FCSTD DOCUMENT  (FreeCAD 0.18R4 (GitTag))
Label: AAM6_Assembled
License: All rights reserved
LicenseURL: http://en.wikipedia.org/wiki/All_rights_reserved
objects: Part::Feature×212, Part::FeaturePython×80, App::DocumentObjectGroup×22, App::Part×19, Part::Sphere×2
note: 294 computed .brp shape members not serialized (recipe doc carries the construction recipe); baked Part::Feature solids carry a one-line shape summary decoded from their .brp

FEATURE [Part::Feature] Body001053  label="D8x380_Rod_001"
  Placement = pos=(-85,-190,7.9) rot=(-1,0,0;1.5708rad)
  shape: bbox 8 x 380 x 8 mm, 5 faces (baked)
FEATURE [Part::Feature] Body001054  label="D8x380_Rod_002"
  Placement = pos=(85,-190,7.9) rot=(-1,0,0;1.5708rad)
  shape: bbox 8 x 380 x 8 mm, 5 faces (baked)
FEATURE [Part::Feature] Body001079  label="CenterMark"
  Placement = pos=(0,-189,17.35) rot=(0,0,1;0rad)
  shape: bbox 0.2 x 390 x 80 mm, 6 faces (baked)
FEATURE [Part::Feature] Fusion011  label="EndstopSwitchY"
  Placement = pos=(64.75,176.5,8.2) rot=(0,0,1;1.5708rad)
  shape: bbox 20.93 x 24.69 x 6.4 mm, 73 faces, 2 solids (baked)
FEATURE [Part::Feature] Fusion012  label="StepperMotorNema017_Y"
  Placement = pos=(0,0,0) rot=(0,0,1;1.5708rad)
  shape: bbox 42 x 54 x 61.2 mm, 83 faces (baked)
FEATURE [Part::Feature] Body001082002  label="EndSwitchDummy"
  Placement = pos=(64.75,162.4,8) rot=(0,0,1;0rad)
  shape: bbox 20 x 17 x 1 mm, 8 faces (baked)
FEATURE [Part::Feature] Body001082005  label="L-Conn_2x2_12xD5_78x78x3_001"
  Placement = pos=(-195.5,13,419) rot=(0.57735,0.57735,-0.57735;2.0944rad)
  shape: bbox 78 x 3 x 78 mm, 24 faces (baked)
FEATURE [Part::Feature] Body001082006  label="L-Conn_2x2_12xD5_78x78x3_002"
  Placement = pos=(195.5,13,419) rot=(0,0.707107,-0.707107;3.14159rad)
  shape: bbox 78 x 3 x 78 mm, 24 faces (baked)
FEATURE [Part::Feature] Body001082007  label="L-Conn_1x1_5xD5_58x58x3_001"
  Placement = pos=(-155.5,189,-23) rot=(0,0,-1;1.5708rad)
  shape: bbox 58 x 58 x 3 mm, 17 faces (baked)
FEATURE [Part::Feature] Body001082008  label="L-Conn_1x1_5xD5_58x58x3_002"
  Placement = pos=(155.5,189,-23) rot=(0,0,1;3.14159rad)
  shape: bbox 58 x 58 x 3 mm, 17 faces (baked)
FEATURE [Part::Feature] Body001082009  label="L-Conn_1x1_5xD5_58x58x3_003"
  Placement = pos=(-155.5,-189,-23) rot=(0,1,0;0rad)
  shape: bbox 58 x 58 x 3 mm, 17 faces (baked)
FEATURE [Part::Feature] Body001082010  label="L-Conn_1x1_5xD5_58x58x3_004"
  Placement = pos=(155.5,-189,-23) rot=(0,0,1;1.5708rad)
  shape: bbox 58 x 58 x 3 mm, 17 faces (baked)
FEATURE [App::DocumentObjectGroup] Group002  label="JointsXY"
  Group = -> [Body001082007,Body001082008,Body001082009,Body001082010]
FEATURE [Part::Feature] Body001082011  label="T-Conn_1x1_5xD5_58x58x3_001"
  Placement = pos=(-137.5,3.1e-14,-23) rot=(0,0,1;1.5708rad)
  shape: bbox 58 x 58 x 3 mm, 19 faces (baked)
FEATURE [Part::Feature] Body001082012  label="T-Conn_1x1_5xD5_58x58x3_002"
  Placement = pos=(137.5,-3.1e-14,-23) rot=(0,0,-1;1.5708rad)
  shape: bbox 58 x 58 x 3 mm, 19 faces (baked)
FEATURE [Part::Feature] Body001082013  label="2040_Nut5_TypI-313_001"
  Placement = pos=(-156.5,-180,0) rot=(0,1,0;1.5708rad)
  shape: bbox 313 x 20 x 40 mm, 120 faces (baked)
FEATURE [Part::Feature] Body001082014  label="2040_Nut5_TypI-313_002"
  Placement = pos=(-156.5,180,0) rot=(0,1,0;1.5708rad)
  shape: bbox 313 x 20 x 40 mm, 120 faces (baked)
FEATURE [Part::Feature] Body001082015  label="2040_Nut5_TypI-313_003"
  Placement = pos=(-156.5,0,400) rot=(0,1,0;1.5708rad)
  shape: bbox 313 x 20 x 40 mm, 120 faces (baked)
FEATURE [Part::Feature] Body001082016  label="2040_Nut5_TypI-340_001"
  Placement = pos=(-146.5,-170,0) rot=(0.57735,-0.57735,-0.57735;4.18879rad)
  shape: bbox 20 x 340 x 40 mm, 120 faces (baked)
FEATURE [Part::Feature] Body001082017  label="2040_Nut5_TypI-340_002"
  Placement = pos=(146.5,-170,0) rot=(0.57735,-0.57735,-0.57735;4.18879rad)
  shape: bbox 20 x 340 x 40 mm, 120 faces (baked)
FEATURE [App::DocumentObjectGroup] Group001  label="ExtrusionsXY"
  Group = -> [Body001082013,Body001082014,Body001082016,Body001082017]
FEATURE [Part::Feature] Body001082018  label="2040_Nut5_TypI-440_001"
  Placement = pos=(-176.5,0,-20) rot=(0,0,1;0rad)
  shape: bbox 40 x 20 x 440 mm, 120 faces (baked)
FEATURE [Part::Feature] Body001082019  label="2040_Nut5_TypI-440_002"
  Placement = pos=(176.5,0,-20) rot=(0,0,1;0rad)
  shape: bbox 40 x 20 x 440 mm, 120 faces (baked)
FEATURE [App::DocumentObjectGroup] Group003  label="ExtrusionsXZ"
  Group = -> [Body001082015,Body001082018,Body001082019]
FEATURE [Part::Feature] Body001082020  label="ISO7380-M5x8_001"
  Placement = pos=(146.5,180,-23) rot=(1,0,0;3.14159rad)
  shape: bbox 9.5 x 9.5 x 10.75 mm, 14 faces (baked)
FEATURE [Part::Feature] Body001082021  label="ISO7380-M5x8_002"
  Placement = pos=(126.5,180,-23) rot=(1,0,0;3.14159rad)
  shape: bbox 9.5 x 9.5 x 10.75 mm, 14 faces (baked)
FEATURE [Part::Feature] Body001082022  label="ISO7380-M5x8_003"
  Placement = pos=(106.5,180,-23) rot=(1,0,0;3.14159rad)
  shape: bbox 9.5 x 9.5 x 10.75 mm, 14 faces (baked)
FEATURE [Part::Feature] Body001082023  label="ISO7380-M5x8_004"
  Placement = pos=(146.5,160,-23) rot=(1,0,0;3.14159rad)
  shape: bbox 9.5 x 9.5 x 10.75 mm, 14 faces (baked)
FEATURE [Part::Feature] Body001082024  label="ISO7380-M5x8_005"
  Placement = pos=(146.5,140,-23) rot=(1,0,0;3.14159rad)
  shape: bbox 9.5 x 9.5 x 10.75 mm, 14 faces (baked)
FEATURE [Part::Feature] Body001082025  label="ISO7380-M5x8_006"
  Placement = pos=(-106.5,180,-23) rot=(1,0,0;3.14159rad)
  shape: bbox 9.5 x 9.5 x 10.75 mm, 14 faces (baked)
FEATURE [Part::Feature] Body001082026  label="ISO7380-M5x8_007"
  Placement = pos=(-126.5,180,-23) rot=(1,0,0;3.14159rad)
  shape: bbox 9.5 x 9.5 x 10.75 mm, 14 faces (baked)
FEATURE [Part::Feature] Body001082027  label="ISO7380-M5x8_008"
  Placement = pos=(-146.5,180,-23) rot=(1,0,0;3.14159rad)
  shape: bbox 9.5 x 9.5 x 10.75 mm, 14 faces (baked)
FEATURE [Part::Feature] Body001082028  label="ISO7380-M5x8_009"
  Placement = pos=(-146.5,160,-23) rot=(1,0,0;3.14159rad)
  shape: bbox 9.5 x 9.5 x 10.75 mm, 14 faces (baked)
FEATURE [Part::Feature] Body001082029  label="ISO7380-M5x8_010"
  Placement = pos=(-146.5,140,-23) rot=(1,0,0;3.14159rad)
  shape: bbox 9.5 x 9.5 x 10.75 mm, 14 faces (baked)
FEATURE [Part::Feature] Body001082030  label="ISO7380-M5x8_021"
  Placement = pos=(146.5,20,-23) rot=(1,0,0;3.14159rad)
  shape: bbox 9.5 x 9.5 x 10.75 mm, 14 faces (baked)
FEATURE [Part::Feature] Body001082031  label="ISO7380-M5x8_022"
  Placement = pos=(186.5,0,-23) rot=(1,0,0;3.14159rad)
  shape: bbox 9.5 x 9.5 x 10.75 mm, 14 faces (baked)
FEATURE [Part::Feature] Body001082032  label="ISO7380-M5x8_023"
  Placement = pos=(166.5,0,-23) rot=(1,0,0;3.14159rad)
  shape: bbox 9.5 x 9.5 x 10.75 mm, 14 faces (baked)
FEATURE [Part::Feature] Body001082033  label="ISO7380-M5x8_024"
  Placement = pos=(146.5,0,-23) rot=(1,0,0;3.14159rad)
  shape: bbox 9.5 x 9.5 x 10.75 mm, 14 faces (baked)
FEATURE [Part::Feature] Body001082034  label="ISO7380-M5x8_025"
  Placement = pos=(146.5,-20,-23) rot=(1,0,0;3.14159rad)
  shape: bbox 9.5 x 9.5 x 10.75 mm, 14 faces (baked)
FEATURE [Part::Feature] Body001082035  label="ISO7380-M5x8_026"
  Placement = pos=(-146.5,20,-23) rot=(1,0,0;3.14159rad)
  shape: bbox 9.5 x 9.5 x 10.75 mm, 14 faces (baked)
FEATURE [Part::Feature] Body001082036  label="ISO7380-M5x8_027"
  Placement = pos=(-146.5,0,-23) rot=(1,0,0;3.14159rad)
  shape: bbox 9.5 x 9.5 x 10.75 mm, 14 faces (baked)
FEATURE [Part::Feature] Body001082037  label="ISO7380-M5x8_028"
  Placement = pos=(-166.5,0,-23) rot=(1,0,0;3.14159rad)
  shape: bbox 9.5 x 9.5 x 10.75 mm, 14 faces (baked)
FEATURE [Part::Feature] Body001082038  label="ISO7380-M5x8_029"
  Placement = pos=(-186.5,0,-23) rot=(1,0,0;3.14159rad)
  shape: bbox 9.5 x 9.5 x 10.75 mm, 14 faces (baked)
FEATURE [Part::Feature] Body001082039  label="ISO7380-M5x8_030"
  Placement = pos=(-146.5,-20,-23) rot=(1,0,0;3.14159rad)
  shape: bbox 9.5 x 9.5 x 10.75 mm, 14 faces (baked)
FEATURE [Part::Feature] Body001082040  label="ISO7380-M5x8_011"
  Placement = pos=(146.5,-140,-23) rot=(1,0,0;3.14159rad)
  shape: bbox 9.5 x 9.5 x 10.75 mm, 14 faces (baked)
FEATURE [Part::Feature] Body001082041  label="ISO7380-M5x8_012"
  Placement = pos=(146.5,-160,-23) rot=(1,0,0;3.14159rad)
  shape: bbox 9.5 x 9.5 x 10.75 mm, 14 faces (baked)
FEATURE [Part::Feature] Body001082042  label="ISO7380-M5x8_013"
  Placement = pos=(146.5,-180,-23) rot=(1,0,0;3.14159rad)
  shape: bbox 9.5 x 9.5 x 10.75 mm, 14 faces (baked)
FEATURE [Part::Feature] Body001082043  label="ISO7380-M5x8_014"
  Placement = pos=(126.5,-180,-23) rot=(1,0,0;3.14159rad)
  shape: bbox 9.5 x 9.5 x 10.75 mm, 14 faces (baked)
FEATURE [Part::Feature] Body001082044  label="ISO7380-M5x8_015"
  Placement = pos=(106.5,-180,-23) rot=(1,0,0;3.14159rad)
  shape: bbox 9.5 x 9.5 x 10.75 mm, 14 faces (baked)
FEATURE [Part::Feature] Body001082045  label="ISO7380-M5x8_016"
  Placement = pos=(-146.5,-140,-23) rot=(1,0,0;3.14159rad)
  shape: bbox 9.5 x 9.5 x 10.75 mm, 14 faces (baked)
FEATURE [Part::Feature] Body001082046  label="ISO7380-M5x8_017"
  Placement = pos=(-146.5,-160,-23) rot=(1,0,0;3.14159rad)
  shape: bbox 9.5 x 9.5 x 10.75 mm, 14 faces (baked)
FEATURE [Part::Feature] Body001082047  label="ISO7380-M5x8_018"
  Placement = pos=(-106.5,-180,-23) rot=(1,0,0;3.14159rad)
  shape: bbox 9.5 x 9.5 x 10.75 mm, 14 faces (baked)
FEATURE [Part::Feature] Body001082048  label="ISO7380-M5x8_019"
  Placement = pos=(-126.5,-180,-23) rot=(1,0,0;3.14159rad)
  shape: bbox 9.5 x 9.5 x 10.75 mm, 14 faces (baked)
FEATURE [Part::Feature] Body001082049  label="ISO7380-M5x8_020"
  Placement = pos=(-146.5,-180,-23) rot=(1,0,0;3.14159rad)
  shape: bbox 9.5 x 9.5 x 10.75 mm, 14 faces (baked)
FEATURE [Part::Feature] Body001082050  label="SlidingT-NutBlock_M5_Slot5_Typ-I_001"
  Placement = pos=(149.5,180,-18.8) rot=(0.57735,0.57735,-0.57735;4.18879rad)
  shape: bbox 12 x 7.7 x 4.6 mm, 21 faces (baked)
FEATURE [Part::Feature] Body001082051  label="SlidingT-NutBlock_M5_Slot5_Typ-I_002"
  Placement = pos=(129.5,180,-18.8) rot=(0.57735,0.57735,-0.57735;4.18879rad)
  shape: bbox 12 x 7.7 x 4.6 mm, 21 faces (baked)
FEATURE [Part::Feature] Body001082052  label="SlidingT-NutBlock_M5_Slot5_Typ-I_003"
  Placement = pos=(109.5,180,-18.8) rot=(0.57735,0.57735,-0.57735;4.18879rad)
  shape: bbox 12 x 7.7 x 4.6 mm, 21 faces (baked)
FEATURE [Part::Feature] Body001082053  label="SlidingT-NutBlock_M5_Slot5_Typ-I_004"
  Placement = pos=(-109.5,180,-18.8) rot=(0.57735,-0.57735,0.57735;4.18879rad)
  shape: bbox 12 x 7.7 x 4.6 mm, 21 faces (baked)
FEATURE [Part::Feature] Body001082054  label="SlidingT-NutBlock_M5_Slot5_Typ-I_005"
  Placement = pos=(-129.5,180,-18.8) rot=(0.57735,-0.57735,0.57735;4.18879rad)
  shape: bbox 12 x 7.7 x 4.6 mm, 21 faces (baked)
FEATURE [Part::Feature] Body001082055  label="SlidingT-NutBlock_M5_Slot5_Typ-I_006"
  Placement = pos=(-149.5,180,-18.8) rot=(0.57735,-0.57735,0.57735;4.18879rad)
  shape: bbox 12 x 7.7 x 4.6 mm, 21 faces (baked)
FEATURE [Part::Feature] Body001082056  label="SlidingT-NutBlock_M5_Slot5_Typ-I_007"
  Placement = pos=(149.5,-180,-18.8) rot=(0.57735,0.57735,-0.57735;4.18879rad)
  shape: bbox 12 x 7.7 x 4.6 mm, 21 faces (baked)
FEATURE [Part::Feature] Body001082057  label="SlidingT-NutBlock_M5_Slot5_Typ-I_008"
  Placement = pos=(129.5,-180,-18.8) rot=(0.57735,0.57735,-0.57735;4.18879rad)
  shape: bbox 12 x 7.7 x 4.6 mm, 21 faces (baked)
FEATURE [Part::Feature] Body001082058  label="SlidingT-NutBlock_M5_Slot5_Typ-I_009"
  Placement = pos=(109.5,-180,-18.8) rot=(0.57735,0.57735,-0.57735;4.18879rad)
  shape: bbox 12 x 7.7 x 4.6 mm, 21 faces (baked)
FEATURE [Part::Feature] Body001082059  label="SlidingT-NutBlock_M5_Slot5_Typ-I_010"
  Placement = pos=(-109.5,-180,-18.8) rot=(0.57735,-0.57735,0.57735;4.18879rad)
  shape: bbox 12 x 7.7 x 4.6 mm, 21 faces (baked)
FEATURE [Part::Feature] Body001082060  label="SlidingT-NutBlock_M5_Slot5_Typ-I_011"
  Placement = pos=(-129.5,-180,-18.8) rot=(0.57735,-0.57735,0.57735;4.18879rad)
  shape: bbox 12 x 7.7 x 4.6 mm, 21 faces (baked)
FEATURE [Part::Feature] Body001082061  label="SlidingT-NutBlock_M5_Slot5_Typ-I_012"
  Placement = pos=(-149.5,-180,-18.8) rot=(0.57735,-0.57735,0.57735;4.18879rad)
  shape: bbox 12 x 7.7 x 4.6 mm, 21 faces (baked)
FEATURE [Part::Feature] Body001082062  label="SlidingT-NutBlock_M5_Slot5_Typ-I_013"
  Placement = pos=(146.5,163,-18.8) rot=(0,0.707107,-0.707107;3.14159rad)
  shape: bbox 7.7 x 12 x 4.6 mm, 21 faces (baked)
FEATURE [Part::Feature] Body001082063  label="SlidingT-NutBlock_M5_Slot5_Typ-I_014"
  Placement = pos=(146.5,143,-18.8) rot=(0,0.707107,-0.707107;3.14159rad)
  shape: bbox 7.7 x 12 x 4.6 mm, 21 faces (baked)
FEATURE [Part::Feature] Body001082064  label="SlidingT-NutBlock_M5_Slot5_Typ-I_015"
  Placement = pos=(-146.5,163,-18.8) rot=(0,-0.707107,0.707107;3.14159rad)
  shape: bbox 7.7 x 12 x 4.6 mm, 21 faces (baked)
FEATURE [Part::Feature] Body001082065  label="SlidingT-NutBlock_M5_Slot5_Typ-I_016"
  Placement = pos=(-146.5,143,-18.8) rot=(0,0.707107,-0.707107;3.14159rad)
  shape: bbox 7.7 x 12 x 4.6 mm, 21 faces (baked)
FEATURE [Part::Feature] Body001082066  label="SlidingT-NutBlock_M5_Slot5_Typ-I_017"
  Placement = pos=(146.5,-143,-18.8) rot=(-1,0,0;1.5708rad)
  shape: bbox 7.7 x 12 x 4.6 mm, 21 faces (baked)
FEATURE [Part::Feature] Body001082067  label="SlidingT-NutBlock_M5_Slot5_Typ-I_018"
  Placement = pos=(146.5,-163,-18.8) rot=(-1,0,0;1.5708rad)
  shape: bbox 7.7 x 12 x 4.6 mm, 21 faces (baked)
FEATURE [Part::Feature] Body001082068  label="SlidingT-NutBlock_M5_Slot5_Typ-I_019"
  Placement = pos=(-146.5,-143,-18.8) rot=(-1,0,0;1.5708rad)
  shape: bbox 7.7 x 12 x 4.6 mm, 21 faces (baked)
FEATURE [Part::Feature] Body001082069  label="SlidingT-NutBlock_M5_Slot5_Typ-I_020"
  Placement = pos=(-146.5,-163,-18.8) rot=(-1,0,0;1.5708rad)
  shape: bbox 7.7 x 12 x 4.6 mm, 21 faces (baked)
FEATURE [App::DocumentObjectGroup] Group  label="Screws&NutsXY"
  Group = -> [Body001082020,Body001082021,Body001082022,Body001082023,Body001082024,Body001082025,Body001082026,Body001082027,Body001082028,Body001082029,Body001082040,Body001082041,Body001082042,Body001082043,Body001082044,Body001082045,Body001082046,Body001082047,Body001082048,Body001082049,Body001082050,Body001082051,Body001082052,Body001082053,Body001082054,Body001082055,Body001082056,Body001082057,+12 more]
FEATURE [App::Part] Part026  label="Y-Frame"
  Group = -> [Group001,Group002,Body001082007,Body001082008,Body001082009,Body001082010,Body001082013,Body001082014,Body001082016,Body001082017,Group,Body001082020,Body001082021,Body001082022,Body001082023,Body001082024,Body001082025,Body001082026,Body001082027,Body001082028,Body001082029,Body001082040,Body001082041,Body001082042,Body001082043,Body001082044,Body001082045,Body001082046,Body001082047,+22 more]
  Origin = -> Origin026
  Placement = pos=(1.33e-14,1.33e-14,0) rot=(0,0.707107,0.707107;0rad)
FEATURE [Part::Feature] Body001082070  label="SlidingT-NutBlock_M5_Slot5_Typ-I_021"
  Placement = pos=(146.5,17,-18.8) rot=(-1,0,0;1.5708rad)
  shape: bbox 7.7 x 12 x 4.6 mm, 21 faces (baked)
FEATURE [Part::Feature] Body001082071  label="SlidingT-NutBlock_M5_Slot5_Typ-I_022"
  Placement = pos=(146.634,-3,-18.8) rot=(-1,0,0;1.5708rad)
  shape: bbox 7.7 x 12 x 4.6 mm, 21 faces (baked)
FEATURE [Part::Feature] Body001082072  label="SlidingT-NutBlock_M5_Slot5_Typ-I_023"
  Placement = pos=(146.5,-23,-18.8) rot=(-1,0,0;1.5708rad)
  shape: bbox 7.7 x 12 x 4.6 mm, 21 faces (baked)
FEATURE [Part::Feature] Body001082073  label="SlidingT-NutBlock_M5_Slot5_Typ-I_024"
  Placement = pos=(-146.5,17,-18.8) rot=(-1,0,0;1.5708rad)
  shape: bbox 7.7 x 12 x 4.6 mm, 21 faces (baked)
FEATURE [Part::Feature] Body001082074  label="SlidingT-NutBlock_M5_Slot5_Typ-I_025"
  Placement = pos=(-146.5,-3,-18.8) rot=(-1,0,0;1.5708rad)
  shape: bbox 7.7 x 12 x 4.6 mm, 21 faces (baked)
FEATURE [Part::Feature] Body001082075  label="SlidingT-NutBlock_M5_Slot5_Typ-I_026"
  Placement = pos=(-146.5,-23,-18.8) rot=(-1,0,0;1.5708rad)
  shape: bbox 7.7 x 12 x 4.6 mm, 21 faces (baked)
FEATURE [Part::Feature] Body001082076  label="ISO7380-M5x8_031"
  Placement = pos=(186.5,13,370) rot=(-1,0,0;1.5708rad)
  shape: bbox 9.5 x 10.75 x 9.5 mm, 14 faces (baked)
FEATURE [Part::Feature] Body001082077  label="ISO7380-M5x8_032"
  Placement = pos=(186.5,13,350) rot=(-1,0,0;1.5708rad)
  shape: bbox 9.5 x 10.75 x 9.5 mm, 14 faces (baked)
FEATURE [Part::Feature] Body001082078  label="ISO7380-M5x8_033"
  Placement = pos=(166.5,13,390) rot=(-1,0,0;1.5708rad)
  shape: bbox 9.5 x 10.75 x 9.5 mm, 14 faces (baked)
FEATURE [Part::Feature] Body001082079  label="ISO7380-M5x8_034"
  Placement = pos=(166.5,13,370) rot=(-1,0,0;1.5708rad)
  shape: bbox 9.5 x 10.75 x 9.5 mm, 14 faces (baked)
FEATURE [Part::Feature] Body001082080  label="ISO7380-M5x8_035"
  Placement = pos=(166.5,13,350) rot=(-1,0,0;1.5708rad)
  shape: bbox 9.5 x 10.75 x 9.5 mm, 14 faces (baked)
FEATURE [Part::Feature] Body001082081  label="ISO7380-M5x8_036"
  Placement = pos=(146.5,13,410) rot=(-1,0,0;1.5708rad)
  shape: bbox 9.5 x 10.75 x 9.5 mm, 14 faces (baked)
FEATURE [Part::Feature] Body001082082  label="ISO7380-M5x8_037"
  Placement = pos=(126.5,13,410) rot=(-1,0,0;1.5708rad)
  shape: bbox 9.5 x 10.75 x 9.5 mm, 14 faces (baked)
FEATURE [Part::Feature] Body001082083  label="ISO7380-M5x8_038"
  Placement = pos=(146.5,13,390) rot=(-1,0,0;1.5708rad)
  shape: bbox 9.5 x 10.75 x 9.5 mm, 14 faces (baked)
FEATURE [Part::Feature] Body001082084  label="ISO7380-M5x8_039"
  Placement = pos=(126.5,13,390) rot=(-1,0,0;1.5708rad)
  shape: bbox 9.5 x 10.75 x 9.5 mm, 14 faces (baked)
FEATURE [Part::Feature] Body001082085  label="ISO7380-M5x8_040"
  Placement = pos=(-126.5,13,410) rot=(-1,0,0;1.5708rad)
  shape: bbox 9.5 x 10.75 x 9.5 mm, 14 faces (baked)
FEATURE [Part::Feature] Body001082086  label="ISO7380-M5x8_041"
  Placement = pos=(-146.5,13,410) rot=(-1,0,0;1.5708rad)
  shape: bbox 9.5 x 10.75 x 9.5 mm, 14 faces (baked)
FEATURE [Part::Feature] Body001082087  label="ISO7380-M5x8_042"
  Placement = pos=(-126.5,13,390) rot=(-1,0,0;1.5708rad)
  shape: bbox 9.5 x 10.75 x 9.5 mm, 14 faces (baked)
FEATURE [Part::Feature] Body001082088  label="ISO7380-M5x8_043"
  Placement = pos=(-146.5,13,390) rot=(-1,0,0;1.5708rad)
  shape: bbox 9.5 x 10.75 x 9.5 mm, 14 faces (baked)
FEATURE [Part::Feature] Body001082089  label="ISO7380-M5x8_044"
  Placement = pos=(-166.5,13,390) rot=(-1,0,0;1.5708rad)
  shape: bbox 9.5 x 10.75 x 9.5 mm, 14 faces (baked)
FEATURE [Part::Feature] Body001082090  label="ISO7380-M5x8_045"
  Placement = pos=(-166.5,13,370) rot=(-1,0,0;1.5708rad)
  shape: bbox 9.5 x 10.75 x 9.5 mm, 14 faces (baked)
FEATURE [Part::Feature] Body001082091  label="ISO7380-M5x8_046"
  Placement = pos=(-186.5,13,370) rot=(-1,0,0;1.5708rad)
  shape: bbox 9.5 x 10.75 x 9.5 mm, 14 faces (baked)
FEATURE [Part::Feature] Body001082092  label="ISO7380-M5x8_047"
  Placement = pos=(-166.5,13,350) rot=(-1,0,0;1.5708rad)
  shape: bbox 9.5 x 10.75 x 9.5 mm, 14 faces (baked)
FEATURE [Part::Feature] Body001082093  label="ISO7380-M5x8_048"
  Placement = pos=(-186.5,13,350) rot=(-1,0,0;1.5708rad)
  shape: bbox 9.5 x 10.75 x 9.5 mm, 14 faces (baked)
FEATURE [Part::Feature] Body001082094  label="SlidingT-NutBlock_M5_Slot5_Typ-I_027"
  Placement = pos=(186.5,8.8,353) rot=(0,1,0;3.14159rad)
  shape: bbox 7.7 x 4.6 x 12 mm, 21 faces (baked)
FEATURE [Part::Feature] Body001082095  label="SlidingT-NutBlock_M5_Slot5_Typ-I_028"
  Placement = pos=(166.5,8.8,353) rot=(0,1,0;3.14159rad)
  shape: bbox 7.7 x 4.6 x 12 mm, 21 faces (baked)
FEATURE [Part::Feature] Body001082096  label="SlidingT-NutBlock_M5_Slot5_Typ-I_029"
  Placement = pos=(186.5,8.8,373) rot=(0,1,0;3.14159rad)
  shape: bbox 7.7 x 4.6 x 12 mm, 21 faces (baked)
FEATURE [Part::Feature] Body001082097  label="SlidingT-NutBlock_M5_Slot5_Typ-I_030"
  Placement = pos=(166.5,8.8,373) rot=(0,1,0;3.14159rad)
  shape: bbox 7.7 x 4.6 x 12 mm, 21 faces (baked)
FEATURE [Part::Feature] Body001082098  label="SlidingT-NutBlock_M5_Slot5_Typ-I_031"
  Placement = pos=(166.5,8.8,393) rot=(0,1,0;3.14159rad)
  shape: bbox 7.7 x 4.6 x 12 mm, 21 faces (baked)
FEATURE [Part::Feature] Body001082099  label="SlidingT-NutBlock_M5_Slot5_Typ-I_032"
  Placement = pos=(149.5,8.8,410) rot=(0,-1,0;1.5708rad)
  shape: bbox 12 x 4.6 x 7.7 mm, 21 faces (baked)
FEATURE [Part::Feature] Body001082100  label="SlidingT-NutBlock_M5_Slot5_Typ-I_033"
  Placement = pos=(129.5,8.8,410) rot=(0,-1,0;1.5708rad)
  shape: bbox 12 x 4.6 x 7.7 mm, 21 faces (baked)
FEATURE [Part::Feature] Body001082101  label="SlidingT-NutBlock_M5_Slot5_Typ-I_034"
  Placement = pos=(149.5,8.8,390) rot=(0,-1,0;1.5708rad)
  shape: bbox 12 x 4.6 x 7.7 mm, 21 faces (baked)
FEATURE [Part::Feature] Body001082102  label="SlidingT-NutBlock_M5_Slot5_Typ-I_035"
  Placement = pos=(129.5,8.8,390) rot=(0,-1,0;1.5708rad)
  shape: bbox 12 x 4.6 x 7.7 mm, 21 faces (baked)
FEATURE [Part::Feature] Body001082103  label="SlidingT-NutBlock_M5_Slot5_Typ-I_036"
  Placement = pos=(-129.5,8.8,410) rot=(0,1,0;1.5708rad)
  shape: bbox 12 x 4.6 x 7.7 mm, 21 faces (baked)
FEATURE [Part::Feature] Body001082104  label="SlidingT-NutBlock_M5_Slot5_Typ-I_037"
  Placement = pos=(-149.5,8.8,410) rot=(0,1,0;1.5708rad)
  shape: bbox 12 x 4.6 x 7.7 mm, 21 faces (baked)
FEATURE [Part::Feature] Body001082105  label="SlidingT-NutBlock_M5_Slot5_Typ-I_038"
  Placement = pos=(-129.5,8.8,390) rot=(0,1,0;1.5708rad)
  shape: bbox 12 x 4.6 x 7.7 mm, 21 faces (baked)
FEATURE [Part::Feature] Body001082106  label="SlidingT-NutBlock_M5_Slot5_Typ-I_039"
  Placement = pos=(-149.5,8.8,390) rot=(0,1,0;1.5708rad)
  shape: bbox 12 x 4.6 x 7.7 mm, 21 faces (baked)
FEATURE [Part::Feature] Body001082107  label="SlidingT-NutBlock_M5_Slot5_Typ-I_040"
  Placement = pos=(-166.5,8.8,393) rot=(0,1,0;3.14159rad)
  shape: bbox 7.7 x 4.6 x 12 mm, 21 faces (baked)
FEATURE [Part::Feature] Body001082108  label="SlidingT-NutBlock_M5_Slot5_Typ-I_041"
  Placement = pos=(-166.5,8.8,373) rot=(0,1,0;3.14159rad)
  shape: bbox 7.7 x 4.6 x 12 mm, 21 faces (baked)
FEATURE [Part::Feature] Body001082109  label="SlidingT-NutBlock_M5_Slot5_Typ-I_042"
  Placement = pos=(-186.5,8.8,373) rot=(0,1,0;3.14159rad)
  shape: bbox 7.7 x 4.6 x 12 mm, 21 faces (baked)
FEATURE [Part::Feature] Body001082110  label="SlidingT-NutBlock_M5_Slot5_Typ-I_043"
  Placement = pos=(-166.5,8.8,353) rot=(0,1,0;3.14159rad)
  shape: bbox 7.7 x 4.6 x 12 mm, 21 faces (baked)
FEATURE [Part::Feature] Body001082111  label="SlidingT-NutBlock_M5_Slot5_Typ-I_044"
  Placement = pos=(-186.5,8.8,353) rot=(0,1,0;3.14159rad)
  shape: bbox 7.7 x 4.6 x 12 mm, 21 faces (baked)
FEATURE [App::DocumentObjectGroup] Group005  label="Screws&NutsXZ"
  Group = -> [Body001082030,Body001082031,Body001082032,Body001082033,Body001082034,Body001082035,Body001082036,Body001082037,Body001082038,Body001082039,Body001082076,Body001082077,Body001082078,Body001082079,Body001082080,Body001082081,Body001082082,Body001082083,Body001082084,Body001082085,Body001082086,Body001082087,Body001082088,Body001082089,Body001082090,Body001082091,Body001082092,Body001082093,+24 more]
FEATURE [Part::Feature] Part__Feature001001  label="Bracket_20x20_Slot5_Type-I_001"
  Placement = pos=(-156.5,1e-14,20) rot=(0,0.707107,0.707107;3.14159rad)
  shape: bbox 19.8 x 18 x 19.8 mm, 174 faces (baked)
FEATURE [Part::Feature] Part__Feature001002  label="Bracket_20x20_Slot5_Type-I_002"
  Placement = pos=(156.5,-4e-15,19.5) rot=(1,0,0;1.5708rad)
  shape: bbox 19.8 x 18 x 19.8 mm, 174 faces (baked)
FEATURE [Part::Feature] Part__Feature001003  label="Bracket_20x40_Slot5_Type-I_001"
  Placement = pos=(156.5,8.4e-14,380) rot=(-1,0,0;1.5708rad)
  shape: bbox 39.5 x 18 x 39.5 mm, 167 faces (baked)
FEATURE [Part::Feature] Part__Feature001004  label="Bracket_20x40_Slot5_Type-I_002"
  Placement = pos=(-156.5,8.4e-14,380) rot=(0.57735,0.57735,0.57735;4.18879rad)
  shape: bbox 39.5 x 18 x 39.5 mm, 167 faces (baked)
FEATURE [Part::Feature] Part__Feature001005  label="Bracket_20x20_Slot5_Type-I_003"
  Placement = pos=(-156.5,10,10) rot=(0,0,1;0rad)
  shape: bbox 19.8 x 19.8 x 18 mm, 174 faces (baked)
FEATURE [Part::Feature] Part__Feature001006  label="Bracket_20x20_Slot5_Type-I_004"
  Placement = pos=(156.5,10,10) rot=(0,0,-1;1.5708rad)
  shape: bbox 19.8 x 19.8 x 18 mm, 174 faces (baked)
FEATURE [App::DocumentObjectGroup] Group004  label="JointsXZ"
  Group = -> [Body001082005,Body001082006,Body001082011,Body001082012,Part__Feature001003,Part__Feature001004,Part__Feature001001,Part__Feature001002,Part__Feature001005,Part__Feature001006]
FEATURE [App::Part] Part027  label="ZX-Frame"
  Group = -> [Group003,Group004,Body001082005,Body001082006,Body001082011,Body001082012,Body001082015,Body001082018,Body001082019,Group005,Body001082030,Body001082031,Body001082032,Body001082033,Body001082034,Body001082035,Body001082036,Body001082037,Body001082038,Body001082039,Body001082070,Body001082071,Body001082072,Body001082073,Body001082074,Body001082075,Body001082076,Body001082077,Body001082078,+39 more]
  Origin = -> Origin027
  Placement = pos=(0,73,0) rot=(0,0,1;0rad)
FEATURE [App::DocumentObjectGroup] Group019  label="Frame"
  Group = -> [Part026,Part027,Body001079]
FEATURE [Part::Feature] Body001082125  label="Strut_horizontal001"
  Placement = pos=(0,0,8) rot=(0,0,1;0rad)
  shape: bbox 218 x 30 x 3 mm, 20 faces (baked)
FEATURE [Part::Feature] Body001082127  label="Strut_vertical004"
  Placement = pos=(0,0,11) rot=(0,0,1;0rad)
  shape: bbox 48 x 218 x 3 mm, 23 faces (baked)
FEATURE [Part::Feature] Body001082126  label="Strut_vertical003"
  Placement = pos=(0,1.3e-14,11) rot=(0,0,1;3.14159rad)
  shape: bbox 48 x 218 x 3 mm, 23 faces (baked)
FEATURE [Part::FeaturePython] Screw004  label="M4x8-Screw059"  # Fasteners workbench fastener (typed FeaturePython)
  Placement = pos=(97,7.5,8) rot=(1,0,0;3.14159rad)
  diameter = 6
  invert = false
  length = 2
  matchOuter = false
  offset = 0
  thread = false
  type = 16
FEATURE [Part::FeaturePython] Screw005  label="M4x8-Screw046"  # Fasteners workbench fastener (typed FeaturePython)
  Placement = pos=(97,-7.5,8) rot=(1,0,0;3.14159rad)
  diameter = 6
  invert = false
  length = 2
  matchOuter = false
  offset = 0
  thread = false
  type = 16
FEATURE [Part::FeaturePython] Screw006  label="M4x8-Screw053"  # Fasteners workbench fastener (typed FeaturePython)
  Placement = pos=(73,2e-15,8) rot=(1,0,0;3.14159rad)
  diameter = 6
  invert = false
  length = 2
  matchOuter = false
  offset = 0
  thread = false
  type = 16
FEATURE [Part::FeaturePython] Screw007  label="M4x8-Screw047"  # Fasteners workbench fastener (typed FeaturePython)
  Placement = pos=(-73,2e-15,8) rot=(1,0,0;3.14159rad)
  diameter = 6
  invert = false
  length = 2
  matchOuter = false
  offset = 0
  thread = false
  type = 16
FEATURE [Part::FeaturePython] Screw008  label="M4x8-Screw057"  # Fasteners workbench fastener (typed FeaturePython)
  Placement = pos=(-97,7.5,8) rot=(1,0,0;3.14159rad)
  diameter = 6
  invert = false
  length = 2
  matchOuter = false
  offset = 0
  thread = false
  type = 16
FEATURE [Part::FeaturePython] Screw009  label="M4x8-Screw052"  # Fasteners workbench fastener (typed FeaturePython)
  Placement = pos=(-97,-7.5,8) rot=(1,0,0;3.14159rad)
  diameter = 6
  invert = false
  length = 2
  matchOuter = false
  offset = 0
  thread = false
  type = 16
FEATURE [Part::FeaturePython] Screw  label="M4x16-Screw004"  # Fasteners workbench fastener (typed FeaturePython)
  Placement = pos=(6,-10,-0.2) rot=(1,0,0;3.14159rad)
  diameter = 6
  invert = false
  length = 6
  matchOuter = false
  offset = 0
  thread = false
  type = 16
FEATURE [Part::FeaturePython] Screw001  label="M4x16-Screw"  # Fasteners workbench fastener (typed FeaturePython)
  Placement = pos=(-6,-10,1) rot=(1,0,0;3.14159rad)
  diameter = 6
  invert = false
  length = 6
  matchOuter = false
  offset = 0
  thread = false
  type = 16
FEATURE [Part::FeaturePython] Screw002  label="M4x16-Screw006"  # Fasteners workbench fastener (typed FeaturePython)
  Placement = pos=(6,10,-0.2) rot=(1,0,0;3.14159rad)
  diameter = 6
  invert = false
  length = 6
  matchOuter = false
  offset = 0
  thread = false
  type = 16
FEATURE [Part::FeaturePython] Screw003  label="M4x16-Screw005"  # Fasteners workbench fastener (typed FeaturePython)
  Placement = pos=(-6,10,1) rot=(1,0,0;3.14159rad)
  diameter = 6
  invert = false
  length = 6
  matchOuter = false
  offset = 0
  thread = false
  type = 16
FEATURE [Part::Feature] Body001082130  label="SC8UU_006"
  shape: bbox 34 x 30 x 22 mm, 79 faces (baked)
FEATURE [Part::Feature] Compound001  label="LM8UU_005"
  Placement = pos=(0,0,0) rot=(-1,0,0;1.5708rad)
  shape: bbox 15 x 24 x 15 mm, 36 faces, 2 solids (baked)
FEATURE [Part::Feature] Body001082128  label="Seeger-RingJ15_009"
  Placement = pos=(0,13,0) rot=(0,1,0;1.0472rad)
  shape: bbox 17.53 x 1 x 17.53 mm, 38 faces (baked)
FEATURE [Part::Feature] Body001082129  label="Seeger-RingJ15_010"
  Placement = pos=(0,-13,0) rot=(0,0,1;0rad)
  shape: bbox 16.94 x 1 x 16.91 mm, 38 faces (baked)
FEATURE [Part::FeaturePython] Screw010  label="M4x8-Screw"  # Fasteners workbench fastener (typed FeaturePython)
  Placement = pos=(-12,9,14) rot=(0,0,1;0rad)
  diameter = 6
  invert = false
  length = 2
  matchOuter = false
  offset = 0
  thread = false
  type = 16
FEATURE [Part::FeaturePython] Screw011  label="M4x8-Screw065"  # Fasteners workbench fastener (typed FeaturePython)
  Placement = pos=(-12,-9,14) rot=(1,0,0;0rad)
  diameter = 6
  invert = false
  length = 2
  matchOuter = false
  offset = 0
  thread = false
  type = 16
FEATURE [Part::FeaturePython] Screw012  label="M4x8-Screw060"  # Fasteners workbench fastener (typed FeaturePython)
  Placement = pos=(12,9,14) rot=(1,0,0;0rad)
  diameter = 6
  invert = false
  length = 2
  matchOuter = false
  offset = 0
  thread = false
  type = 16
FEATURE [Part::FeaturePython] Screw013  label="M4x8-Screw056"  # Fasteners workbench fastener (typed FeaturePython)
  Placement = pos=(12,-9,14) rot=(1,0,0;0rad)
  diameter = 6
  invert = false
  length = 2
  matchOuter = false
  offset = 0
  thread = false
  type = 16
FEATURE [App::Part] Part049  label="SCS8UU_008"
  Group = -> [Body001082130,Compound001,Body001082128,Body001082129,Screw010,Screw011,Screw012,Screw013]
  Origin = -> Origin056
  Placement = pos=(-85,-37,0) rot=(0,0,1;0rad)
FEATURE [Part::Feature] Body001082124  label="SC8UU_005"
  shape: bbox 34 x 30 x 22 mm, 79 faces (baked)
FEATURE [Part::Feature] Compound002  label="LM8UU_006"
  Placement = pos=(0,0,0) rot=(-1,0,0;1.5708rad)
  shape: bbox 15 x 24 x 15 mm, 36 faces, 2 solids (baked)
FEATURE [Part::Feature] Body001082132  label="Seeger-RingJ15_012"
  Placement = pos=(0,-13,0) rot=(0,1,0;3.66519rad)
  shape: bbox 16.94 x 1 x 16.96 mm, 38 faces (baked)
FEATURE [Part::Feature] Body001082131  label="Seeger-RingJ15_011"
  Placement = pos=(0,13,0) rot=(0,-1,0;1.8326rad)
  shape: bbox 17.24 x 1 x 16.94 mm, 38 faces (baked)
FEATURE [Part::FeaturePython] Screw014  label="M4x8-Screw063"  # Fasteners workbench fastener (typed FeaturePython)
  Placement = pos=(-12,9,14) rot=(1,0,0;0rad)
  diameter = 6
  invert = false
  length = 2
  matchOuter = false
  offset = 0
  thread = false
  type = 16
FEATURE [Part::FeaturePython] Screw015  label="M4x8-Screw049"  # Fasteners workbench fastener (typed FeaturePython)
  Placement = pos=(-12,-9,14) rot=(1,0,0;0rad)
  diameter = 6
  invert = false
  length = 2
  matchOuter = false
  offset = 0
  thread = false
  type = 16
FEATURE [Part::FeaturePython] Screw016  label="M4x8-Screw051"  # Fasteners workbench fastener (typed FeaturePython)
  Placement = pos=(12,9,14) rot=(1,0,0;0rad)
  diameter = 6
  invert = false
  length = 2
  matchOuter = false
  offset = 0
  thread = false
  type = 16
FEATURE [Part::FeaturePython] Screw017  label="M4x8-Screw058"  # Fasteners workbench fastener (typed FeaturePython)
  Placement = pos=(12,-9,14) rot=(1,0,0;0rad)
  diameter = 6
  invert = false
  length = 2
  matchOuter = false
  offset = 0
  thread = false
  type = 16
FEATURE [App::Part] Part047  label="SCS8UU_007"
  Group = -> [Body001082124,Compound002,Body001082132,Body001082131,Screw014,Screw015,Screw016,Screw017]
  Origin = -> Origin054
  Placement = pos=(-85,37,0) rot=(0,0,1;0rad)
FEATURE [Part::Feature] Body001082137  label="SC8UU_007"
  shape: bbox 34 x 30 x 22 mm, 79 faces (baked)
FEATURE [Part::Feature] Compound003  label="LM8UU_007"
  Placement = pos=(0,0,0) rot=(-1,0,0;1.5708rad)
  shape: bbox 15 x 24 x 15 mm, 36 faces, 2 solids (baked)
FEATURE [Part::Feature] Body001082133  label="Seeger-RingJ15_013"
  Placement = pos=(0,-13,0) rot=(0,-1,0;1.8326rad)
  shape: bbox 17.24 x 1 x 16.94 mm, 38 faces (baked)
FEATURE [Part::Feature] Body001082134  label="Seeger-RingJ15_014"
  Placement = pos=(0,13,0) rot=(0,1,0;0.785398rad)
  shape: bbox 16.94 x 1 x 16.94 mm, 38 faces (baked)
FEATURE [Part::FeaturePython] Screw018  label="M4x8-Screw061"  # Fasteners workbench fastener (typed FeaturePython)
  Placement = pos=(-12,9,14) rot=(1,0,0;0rad)
  diameter = 6
  invert = false
  length = 2
  matchOuter = false
  offset = 0
  thread = false
  type = 16
FEATURE [Part::FeaturePython] Screw019  label="M4x8-Screw064"  # Fasteners workbench fastener (typed FeaturePython)
  Placement = pos=(-12,-9,14) rot=(1,0,0;0rad)
  diameter = 6
  invert = false
  length = 2
  matchOuter = false
  offset = 0
  thread = false
  type = 16
FEATURE [Part::FeaturePython] Screw020  label="M4x8-Screw055"  # Fasteners workbench fastener (typed FeaturePython)
  Placement = pos=(12,9,14) rot=(1,0,0;0rad)
  diameter = 6
  invert = false
  length = 2
  matchOuter = false
  offset = 0
  thread = false
  type = 16
FEATURE [Part::FeaturePython] Screw021  label="M4x8-Screw050"  # Fasteners workbench fastener (typed FeaturePython)
  Placement = pos=(12,-9,14) rot=(1,0,0;0rad)
  diameter = 6
  invert = false
  length = 2
  matchOuter = false
  offset = 0
  thread = false
  type = 16
FEATURE [App::Part] Part045  label="SCS8UU_005"
  Group = -> [Body001082137,Compound003,Body001082133,Body001082134,Screw018,Screw019,Screw020,Screw021]
  Origin = -> Origin055
  Placement = pos=(85,37,0) rot=(0,0,1;0rad)
FEATURE [Part::Feature] Body001082141  label="SC8UU_008"
  shape: bbox 34 x 30 x 22 mm, 79 faces (baked)
FEATURE [Part::Feature] Compound004  label="LM8UU_008"
  Placement = pos=(0,0,0) rot=(-1,0,0;1.5708rad)
  shape: bbox 15 x 24 x 15 mm, 36 faces, 2 solids (baked)
FEATURE [Part::Feature] Body001082135  label="Seeger-RingJ15_015"
  Placement = pos=(0,13,0) rot=(0,1,0;2.35619rad)
  shape: bbox 16.94 x 1 x 16.94 mm, 38 faces (baked)
FEATURE [Part::Feature] Body001082139  label="Seeger-RingJ15_016"
  Placement = pos=(0,-13,0) rot=(0,1,0;1.5708rad)
  shape: bbox 16.91 x 1 x 16.94 mm, 38 faces (baked)
FEATURE [Part::FeaturePython] Screw022  label="M4x8-Screw054"  # Fasteners workbench fastener (typed FeaturePython)
  Placement = pos=(-12,9,14) rot=(1,0,0;0rad)
  diameter = 6
  invert = false
  length = 2
  matchOuter = false
  offset = 0
  thread = false
  type = 16
FEATURE [Part::FeaturePython] Screw023  label="M4x8-Screw066"  # Fasteners workbench fastener (typed FeaturePython)
  Placement = pos=(-12,-9,14) rot=(1,0,0;0rad)
  diameter = 6
  invert = false
  length = 2
  matchOuter = false
  offset = 0
  thread = false
  type = 16
FEATURE [Part::FeaturePython] Screw024  label="M4x8-Screw048"  # Fasteners workbench fastener (typed FeaturePython)
  Placement = pos=(12,9,14) rot=(1,0,0;0rad)
  diameter = 6
  invert = false
  length = 2
  matchOuter = false
  offset = 0
  thread = false
  type = 16
FEATURE [Part::FeaturePython] Screw025  label="M4x8-Screw062"  # Fasteners workbench fastener (typed FeaturePython)
  Placement = pos=(12,-9,14) rot=(1,0,0;0rad)
  diameter = 6
  invert = false
  length = 2
  matchOuter = false
  offset = 0
  thread = false
  type = 16
FEATURE [App::Part] Part046  label="SCS8UU_006"
  Group = -> [Body001082141,Compound004,Body001082135,Body001082139,Screw022,Screw023,Screw024,Screw025]
  Origin = -> Origin053
  Placement = pos=(85,-37,0) rot=(0,0,1;0rad)
FEATURE [App::DocumentObjectGroup] Group009  label="Linear-Bearings001"
  Group = -> [Part049,Part047,Part045,Part046]
FEATURE [Part::Feature] Fusion013  label="heat-plate_220x220"
  Placement = pos=(0,0,32) rot=(0,0,1;1.5708rad)
  shape: bbox 236.7 x 220 x 10.5 mm, 302 faces (baked)
FEATURE [Part::FeaturePython] Screw026  label="M3x30-Screw"  # Fasteners workbench fastener (typed FeaturePython)
  Placement = pos=(-104.5,104.5,34.5) rot=(0,0,1;0rad)
  diameter = 4
  invert = false
  length = 10
  matchOuter = false
  offset = 0
  thread = false
  type = 17
FEATURE [Part::FeaturePython] Screw027  label="M3x30-Screw008"  # Fasteners workbench fastener (typed FeaturePython)
  Placement = pos=(104.5,104.5,34.5) rot=(0,0,1;0rad)
  diameter = 4
  invert = false
  length = 10
  matchOuter = false
  offset = 0
  thread = false
  type = 17
FEATURE [Part::FeaturePython] Screw028  label="M3x30-Screw006"  # Fasteners workbench fastener (typed FeaturePython)
  Placement = pos=(-104.5,-104.5,34.5) rot=(0,0,1;0rad)
  diameter = 4
  invert = false
  length = 10
  matchOuter = false
  offset = 0
  thread = false
  type = 17
FEATURE [Part::FeaturePython] Screw029  label="M3x30-Screw007"  # Fasteners workbench fastener (typed FeaturePython)
  Placement = pos=(104.5,-104.5,34.5) rot=(0,0,1;0rad)
  diameter = 4
  invert = false
  length = 10
  matchOuter = false
  offset = 0
  thread = false
  type = 17
FEATURE [Part::FeaturePython] Nut  label="M3-Nut"  # Fasteners workbench fastener (typed FeaturePython)
  Placement = pos=(-104.5,104.5,29.6) rot=(0,0,1;0rad)
  diameter = 4
  invert = false
  matchOuter = false
  offset = 0
  thread = false
  type = 4
FEATURE [Part::FeaturePython] Nut001  label="M3-Nut029"  # Fasteners workbench fastener (typed FeaturePython)
  Placement = pos=(104.5,104.5,29.6) rot=(0,0,1;0rad)
  diameter = 4
  invert = false
  matchOuter = false
  offset = 0
  thread = false
  type = 4
FEATURE [Part::FeaturePython] Nut002  label="M3-Nut028"  # Fasteners workbench fastener (typed FeaturePython)
  Placement = pos=(-104.5,-104.5,29.6) rot=(0,0,1;0rad)
  diameter = 4
  invert = false
  matchOuter = false
  offset = 0
  thread = false
  type = 4
FEATURE [Part::FeaturePython] Nut003  label="M3-Nut030"  # Fasteners workbench fastener (typed FeaturePython)
  Placement = pos=(104.5,-104.5,29.6) rot=(0,0,1;0rad)
  diameter = 4
  invert = false
  matchOuter = false
  offset = 0
  thread = false
  type = 4
FEATURE [Part::Feature] Body001082142  label="Spring_8x1x24/18_001"
  Placement = pos=(104.5,104.5,14) rot=(0,0,1;0rad)
  shape: bbox 8.219 x 8.219 x 18.9 mm, 12 faces (baked)
FEATURE [Part::Feature] Body001082138  label="Spring_8x1x24/18_002"
  Placement = pos=(-104.5,104.5,14) rot=(0,0,1;0rad)
  shape: bbox 8.219 x 8.219 x 18.9 mm, 12 faces (baked)
FEATURE [Part::Feature] Body001082144  label="Spring_8x1x24/18_003"
  Placement = pos=(104.5,-104.5,14) rot=(0,0,1;0rad)
  shape: bbox 8.219 x 8.219 x 18.9 mm, 12 faces (baked)
FEATURE [Part::Feature] Body001082146  label="Spring_8x1x24/18_004"
  Placement = pos=(-104.5,-104.5,14) rot=(0,0,1;0rad)
  shape: bbox 8.219 x 8.219 x 18.9 mm, 12 faces (baked)
FEATURE [Part::Feature] Body001082143  label="Thumb-Wheel_M4_007"
  Placement = pos=(-104.5,-104.5,1.5) rot=(0,0,1;0rad)
  shape: bbox 16 x 16 x 9.5 mm, 281 faces (baked)
FEATURE [Part::Feature] Body001082140  label="Thumb-Wheel_M4_006"
  Placement = pos=(-104.5,104.5,1.5) rot=(0,0,1;0rad)
  shape: bbox 16 x 16 x 9.5 mm, 281 faces (baked)
FEATURE [Part::Feature] Body001082145  label="Thumb-Wheel_M4_008"
  Placement = pos=(104.5,104.5,1.5) rot=(0,0,1;0rad)
  shape: bbox 16 x 16 x 9.5 mm, 281 faces (baked)
FEATURE [Part::Feature] Body001082136  label="Thumb-Wheel_M4_005"
  Placement = pos=(104.5,-104.5,1.5) rot=(0,0,1;0rad)
  shape: bbox 16 x 16 x 9.5 mm, 281 faces (baked)
FEATURE [App::DocumentObjectGroup] Group012  label="heated_bed"
  Group = -> [Fusion013,Screw026,Screw027,Screw028,Screw029,Nut,Nut001,Nut002,Nut003,Body001082142,Body001082138,Body001082144,Body001082146,Body001082143,Body001082140,Body001082145,Body001082136]
FEATURE [Part::Feature] Body007  label="LMH8LUU_001"
  Placement = pos=(0,0,17) rot=(0,0,1;0rad)
  shape: bbox 21 x 32 x 45 mm, 30 faces (baked)
FEATURE [Part::Feature] Body009  label="TR-NutWithFlange_001"
  Placement = pos=(23,0,15) rot=(0,0,1;0rad)
  shape: bbox 22.25 x 22.25 x 15.8 mm, 42 faces (baked)
FEATURE [Part::FeaturePython] Screw039  label="M3x16-Screw085"  # Fasteners workbench fastener (typed FeaturePython)
  Placement = pos=(31,0,18.8) rot=(0,0,1;0rad)
  diameter = 4
  invert = false
  length = 6
  matchOuter = false
  offset = 0
  thread = false
  type = 15
FEATURE [Part::FeaturePython] Screw032  label="M3x16-Screw087"  # Fasteners workbench fastener (typed FeaturePython)
  Placement = pos=(23,8,18.8) rot=(0,0,1;0rad)
  diameter = 4
  invert = false
  length = 6
  matchOuter = false
  offset = 0
  thread = false
  type = 15
FEATURE [Part::FeaturePython] Screw041  label="M3x16-Screw088"  # Fasteners workbench fastener (typed FeaturePython)
  Placement = pos=(23,-8,18.8) rot=(0,0,1;0rad)
  diameter = 4
  invert = false
  length = 6
  matchOuter = false
  offset = 0
  thread = false
  type = 15
FEATURE [Part::FeaturePython] Screw042  label="M3x16-Screw078"  # Fasteners workbench fastener (typed FeaturePython)
  Placement = pos=(15,0,18.8) rot=(0,0,1;0rad)
  diameter = 4
  invert = false
  length = 6
  matchOuter = false
  offset = 0
  thread = false
  type = 15
FEATURE [Part::FeaturePython] Screw043  label="M3x16-Screw083"  # Fasteners workbench fastener (typed FeaturePython)
  Placement = pos=(0,12,19) rot=(0,0,1;0rad)
  diameter = 4
  invert = false
  length = 6
  matchOuter = false
  offset = 0
  thread = false
  type = 15
FEATURE [Part::FeaturePython] Screw030  label="M3x16-Screw084"  # Fasteners workbench fastener (typed FeaturePython)
  Placement = pos=(0,-12,19) rot=(0,0,1;0rad)
  diameter = 4
  invert = false
  length = 6
  matchOuter = false
  offset = 0
  thread = false
  type = 15
FEATURE [Part::FeaturePython] Nut005  label="M3-Nut075"  # Fasteners workbench fastener (typed FeaturePython)
  Placement = pos=(23,8,3.2) rot=(0,0,1;0rad)
  diameter = 4
  invert = false
  matchOuter = false
  offset = 0
  thread = false
  type = 4
FEATURE [Part::FeaturePython] Nut015  label="M3-Nut072"  # Fasteners workbench fastener (typed FeaturePython)
  Placement = pos=(31,0,3.2) rot=(0,0,-1;0.523599rad)
  diameter = 4
  invert = false
  matchOuter = false
  offset = 0
  thread = false
  type = 4
FEATURE [Part::FeaturePython] Nut004  label="M3-Nut074"  # Fasteners workbench fastener (typed FeaturePython)
  Placement = pos=(23,-8,3.2) rot=(0,0,1;0rad)
  diameter = 4
  invert = false
  matchOuter = false
  offset = 0
  thread = false
  type = 4
FEATURE [Part::FeaturePython] Nut017  label="M3-Nut073"  # Fasteners workbench fastener (typed FeaturePython)
  Placement = pos=(15,0,3.2) rot=(0,0,-1;0.523599rad)
  diameter = 4
  invert = false
  matchOuter = false
  offset = 0
  thread = false
  type = 4
FEATURE [Part::FeaturePython] Nut018  label="M3-Nut070"  # Fasteners workbench fastener (typed FeaturePython)
  Placement = pos=(0,12,3.2) rot=(0,0,1;0rad)
  diameter = 4
  invert = false
  matchOuter = false
  offset = 0
  thread = false
  type = 4
FEATURE [Part::FeaturePython] Nut006  label="M3-Nut071"  # Fasteners workbench fastener (typed FeaturePython)
  Placement = pos=(0,-12,3.2) rot=(0,0,1;0rad)
  diameter = 4
  invert = false
  matchOuter = false
  offset = 0
  thread = false
  type = 4
FEATURE [App::DocumentObjectGroup] Group015  label="Screws,Nuts,Bearing_Left"
  Group = -> [Body007,Body009,Screw039,Screw032,Screw041,Screw042,Screw043,Screw030,Nut005,Nut015,Nut004,Nut017,Nut018,Nut006]
FEATURE [Part::Feature] Body037001  label="Carriage_Left"
  shape: bbox 62.5 x 111 x 29.5 mm, 165 faces (baked)
FEATURE [Part::Feature] Body036001  label="MotorHolder"
  shape: bbox 104.8 x 34 x 48 mm, 60 faces (baked)
FEATURE [App::Part] Part002  label="Z-Carriage_Left"
  Group = -> [Group015,Body007,Body009,Screw039,Screw032,Screw041,Screw042,Screw043,Screw030,Nut005,Nut015,Nut004,Nut017,Nut018,Nut006,Body037001,Body036001]
  Origin = -> Origin002
  Placement = pos=(-203,0,0) rot=(0,0,1;0rad)
FEATURE [Part::Feature] Body010  label="LMH8LUU_002"
  Placement = pos=(0,0,17) rot=(0,0,1;0rad)
  shape: bbox 21 x 32 x 45 mm, 30 faces (baked)
FEATURE [Part::Feature] Body011  label="TR-NutWithFlange_002"
  Placement = pos=(-23,0,15) rot=(0,0,1;0rad)
  shape: bbox 22.25 x 22.25 x 15.8 mm, 42 faces (baked)
FEATURE [Part::FeaturePython] Screw035  label="M3x16-Screw086"  # Fasteners workbench fastener (typed FeaturePython)
  Placement = pos=(-31,0,18.8) rot=(0,0,1;0rad)
  diameter = 4
  invert = false
  length = 6
  matchOuter = false
  offset = 0
  thread = false
  type = 15
FEATURE [Part::FeaturePython] Screw038  label="M3x16-Screw082"  # Fasteners workbench fastener (typed FeaturePython)
  Placement = pos=(-23,8,18.8) rot=(0,0,1;0rad)
  diameter = 4
  invert = false
  length = 6
  matchOuter = false
  offset = 0
  thread = false
  type = 15
FEATURE [Part::FeaturePython] Screw031  label="M3x16-Screw081"  # Fasteners workbench fastener (typed FeaturePython)
  Placement = pos=(-15,0,18.8) rot=(0,0,1;0rad)
  diameter = 4
  invert = false
  length = 6
  matchOuter = false
  offset = 0
  thread = false
  type = 15
FEATURE [Part::FeaturePython] Screw044  label="M3x16-Screw080"  # Fasteners workbench fastener (typed FeaturePython)
  Placement = pos=(-23,-8,18.8) rot=(0,0,1;0rad)
  diameter = 4
  invert = false
  length = 6
  matchOuter = false
  offset = 0
  thread = false
  type = 15
FEATURE [Part::FeaturePython] Screw036  label="M3x16-Screw079"  # Fasteners workbench fastener (typed FeaturePython)
  Placement = pos=(0,12,19) rot=(0,0,1;0rad)
  diameter = 4
  invert = false
  length = 6
  matchOuter = false
  offset = 0
  thread = false
  type = 15
FEATURE [Part::FeaturePython] Screw040  label="M3x16-Screw077"  # Fasteners workbench fastener (typed FeaturePython)
  Placement = pos=(0,-12,19) rot=(0,0,1;0rad)
  diameter = 4
  invert = false
  length = 6
  matchOuter = false
  offset = 0
  thread = false
  type = 15
FEATURE [Part::FeaturePython] Nut016  label="M3-Nut065"  # Fasteners workbench fastener (typed FeaturePython)
  Placement = pos=(-31,0,3.2) rot=(0,0,-1;0.523599rad)
  diameter = 4
  invert = false
  matchOuter = false
  offset = 0
  thread = false
  type = 4
FEATURE [Part::FeaturePython] Nut007  label="M3-Nut069"  # Fasteners workbench fastener (typed FeaturePython)
  Placement = pos=(-23,8,3.2) rot=(0,0,1;0rad)
  diameter = 4
  invert = false
  matchOuter = false
  offset = 0
  thread = false
  type = 4
FEATURE [Part::FeaturePython] Nut008  label="M3-Nut062"  # Fasteners workbench fastener (typed FeaturePython)
  Placement = pos=(-15,0,3.2) rot=(0,0,-1;0.523599rad)
  diameter = 4
  invert = false
  matchOuter = false
  offset = 0
  thread = false
  type = 4
FEATURE [Part::FeaturePython] Nut009  label="M3-Nut064"  # Fasteners workbench fastener (typed FeaturePython)
  Placement = pos=(-23,-8,3.2) rot=(0,0,1;0rad)
  diameter = 4
  invert = false
  matchOuter = false
  offset = 0
  thread = false
  type = 4
FEATURE [Part::FeaturePython] Nut010  label="M3-Nut061"  # Fasteners workbench fastener (typed FeaturePython)
  Placement = pos=(0,12,3.2) rot=(0,0,1;0rad)
  diameter = 4
  invert = false
  matchOuter = false
  offset = 0
  thread = false
  type = 4
FEATURE [Part::FeaturePython] Nut011  label="M3-Nut068"  # Fasteners workbench fastener (typed FeaturePython)
  Placement = pos=(0,-12,3.2) rot=(0,0,1;0rad)
  diameter = 4
  invert = false
  matchOuter = false
  offset = 0
  thread = false
  type = 4
FEATURE [Part::FeaturePython] Screw033  label="M3x16-Screw"  # Fasteners workbench fastener (typed FeaturePython)
  Placement = pos=(-15,32.5,-4e-15) rot=(-1,0,0;1.5708rad)
  diameter = 4
  invert = false
  length = 7
  matchOuter = false
  offset = 0
  thread = false
  type = 16
FEATURE [Part::FeaturePython] Nut012  label="M3-Nut066"  # Fasteners workbench fastener (typed FeaturePython)
  Placement = pos=(-15,17.1,-4e-15) rot=(-1,0,0;1.5708rad)
  diameter = 4
  invert = false
  matchOuter = false
  offset = 0
  thread = false
  type = 4
FEATURE [Part::FeaturePython] Screw037  label="M3x10-Screw001"  # Fasteners workbench fastener (typed FeaturePython)
  Placement = pos=(18,40,14.1) rot=(0,0,1;0rad)
  diameter = 4
  invert = false
  length = 4
  matchOuter = false
  offset = 0
  thread = false
  type = 16
FEATURE [Part::FeaturePython] Screw034  label="M3x10-Screw"  # Fasteners workbench fastener (typed FeaturePython)
  Placement = pos=(18,-40,14.1) rot=(0,0,1;0rad)
  diameter = 4
  invert = false
  length = 4
  matchOuter = false
  offset = 0
  thread = false
  type = 16
FEATURE [Part::FeaturePython] Nut013  label="M3-Nut063"  # Fasteners workbench fastener (typed FeaturePython)
  Placement = pos=(18,40,6.3) rot=(0,0,1;0rad)
  diameter = 4
  invert = false
  matchOuter = false
  offset = 0
  thread = false
  type = 4
FEATURE [Part::FeaturePython] Nut014  label="M3-Nut067"  # Fasteners workbench fastener (typed FeaturePython)
  Placement = pos=(18,-40,6.3) rot=(0,0,1;0rad)
  diameter = 4
  invert = false
  matchOuter = false
  offset = 0
  thread = false
  type = 4
FEATURE [Part::FeaturePython] Screw045  label="M4x35-Screw"  # Fasteners workbench fastener (typed FeaturePython)
  Placement = pos=(-4,26,3e-15) rot=(0,-1,0;1.5708rad)
  diameter = 6
  invert = false
  length = 9
  matchOuter = false
  offset = 0
  thread = false
  type = 14
FEATURE [Part::FeaturePython] Nut019  label="M4-Nut"  # Fasteners workbench fastener (typed FeaturePython)
  Placement = pos=(30.2,26,-1e-15) rot=(-0.250563,-0.935113,0.250563;1.63783rad)
  diameter = 6
  invert = false
  matchOuter = false
  offset = 0
  thread = false
  type = 4
FEATURE [App::DocumentObjectGroup] Group016  label="Screws,Nuts,Bearing_Right"
  Group = -> [Body010,Body011,Screw035,Screw038,Screw031,Screw044,Screw036,Screw040,Nut016,Nut007,Nut008,Nut009,Nut010,Nut011,Screw033,Nut012,Screw037,Screw034,Nut013,Nut014,Screw045,Nut019]
FEATURE [Part::Feature] Body037002  label="Carriage_Right"
  shape: bbox 68 x 104 x 29 mm, 222 faces (baked)
FEATURE [Part::Feature] Body001082147  label="Tensioner_IdlerHolder_Bolt"
  Placement = pos=(0,26,0) rot=(0,-1,0;1.5708rad)
  shape: bbox 22 x 17 x 14 mm, 24 faces (baked)
FEATURE [Part::Feature] Body001078001  label="Tensioner_IdlerHolder_Screw"
  Placement = pos=(0,26,0) rot=(0,-1,0;1.5708rad)
  shape: bbox 22 x 17 x 14 mm, 33 faces (baked)
FEATURE [Part::Feature] Body001081001  label="Tensioner_AdjustingWheel"
  Placement = pos=(24,26,-5e-15) rot=(0,1,0;1.5708rad)
  shape: bbox 8 x 18 x 18 mm, 95 faces (baked)
FEATURE [App::Part] Part003  label="Z-Carriage_Right"
  Group = -> [Group016,Body010,Body011,Screw035,Screw038,Screw031,Screw044,Screw036,Screw040,Nut016,Nut007,Nut008,Nut009,Nut010,Nut011,Screw033,Nut012,Screw037,Screw034,Nut013,Nut014,Body037002,Body001082147,Body001078001,Body001081001,Screw045,Nut019]
  Origin = -> Origin003
  Placement = pos=(203,0,0) rot=(0,0,1;0rad)
FEATURE [Part::FeaturePython] Screw046  label="M3x10-Screw_002"  # Fasteners workbench fastener (typed FeaturePython)
  Placement = pos=(-23,-15.85,4.1) rot=(0,-1,0;1.5708rad)
  diameter = 4
  invert = false
  length = 4
  matchOuter = false
  offset = 0
  thread = false
  type = 17
FEATURE [Part::FeaturePython] Screw047  label="M3x6-Screw_002"  # Fasteners workbench fastener (typed FeaturePython)
  Placement = pos=(-19.5,46.8,11.5) rot=(0,0,1;0rad)
  diameter = 4
  invert = false
  length = 2
  matchOuter = false
  offset = 0
  thread = false
  type = 17
FEATURE [Part::FeaturePython] Screw048  label="M2x10-Screw"  # Fasteners workbench fastener (typed FeaturePython)
  Placement = pos=(-24.6,44.4,18.3) rot=(0,0,1;0rad)
  diameter = 2
  invert = false
  length = 5
  matchOuter = false
  offset = 0
  thread = false
  type = 18
FEATURE [Part::FeaturePython] Screw049  label="M2x10-Screw_001"  # Fasteners workbench fastener (typed FeaturePython)
  Placement = pos=(-24.6,35.1,18.3) rot=(0,0,1;0rad)
  diameter = 2
  invert = false
  length = 5
  matchOuter = false
  offset = 0
  thread = false
  type = 18
FEATURE [Part::FeaturePython] Washer  label="M3-Washer_001"  # Fasteners workbench fastener (typed FeaturePython)
  Placement = pos=(22,-36.8,14.5) rot=(-1,0,0;1.5708rad)
  diameter = 4
  invert = false
  matchOuter = false
  offset = 0
  type = 2
FEATURE [Part::FeaturePython] Washer001  label="M3-Washer_002"  # Fasteners workbench fastener (typed FeaturePython)
  Placement = pos=(-10,-36.8,14.5) rot=(-1,0,0;1.5708rad)
  diameter = 4
  invert = false
  matchOuter = false
  offset = 0
  type = 2
FEATURE [Part::FeaturePython] Screw050  label="M3x25-Screw_001"  # Fasteners workbench fastener (typed FeaturePython)
  Placement = pos=(-38.4,-1.2,53.4) rot=(0,-1,0;1.5708rad)
  diameter = 4
  invert = false
  length = 9
  matchOuter = false
  offset = 0
  thread = false
  type = 17
FEATURE [Part::FeaturePython] Screw051  label="M3x25-Screw_002"  # Fasteners workbench fastener (typed FeaturePython)
  Placement = pos=(-38.4,-44.2,15.4) rot=(0,-1,0;1.5708rad)
  diameter = 4
  invert = false
  length = 9
  matchOuter = false
  offset = 0
  thread = false
  type = 17
FEATURE [Part::FeaturePython] Nut020  label="M3-Nut_001"  # Fasteners workbench fastener (typed FeaturePython)
  Placement = pos=(-18,-44.2,15.4) rot=(0,1,0;1.5708rad)
  diameter = 4
  invert = false
  matchOuter = false
  offset = 0
  thread = false
  type = 4
FEATURE [Part::FeaturePython] Nut021  label="M3-Nut_002"  # Fasteners workbench fastener (typed FeaturePython)
  Placement = pos=(-18,-1.2,53.4) rot=(0,1,0;1.5708rad)
  diameter = 4
  invert = false
  matchOuter = false
  offset = 0
  thread = false
  type = 4
FEATURE [Part::FeaturePython] Screw052  label="M3x10-Screw_001"  # Fasteners workbench fastener (typed FeaturePython)
  Placement = pos=(-23,-22.85,4.1) rot=(0,-1,0;1.5708rad)
  diameter = 4
  invert = false
  length = 4
  matchOuter = false
  offset = 0
  thread = false
  type = 17
FEATURE [Part::FeaturePython] Screw053  label="M3x6-Screw_001"  # Fasteners workbench fastener (typed FeaturePython)
  Placement = pos=(-19.5,32.9,11.5) rot=(0,0,1;0rad)
  diameter = 4
  invert = false
  length = 2
  matchOuter = false
  offset = 0
  thread = false
  type = 17
FEATURE [Part::Feature] Body001082149  label="AluSled"
  shape: bbox 45 x 100 x 19 mm, 54 faces (baked)
FEATURE [Part::Feature] Compound005  label="LM8LUU_003"
  Placement = pos=(0,-40,0) rot=(0,1,0;1.5708rad)
  shape: bbox 45 x 15 x 15 mm, 36 faces, 2 solids (baked)
FEATURE [Part::Feature] Body001082150  label="EndSwitch_X-Holder"
  Placement = pos=(-19.5,39.85,9) rot=(0,0,1;0rad)
  shape: bbox 19.8 x 20.3 x 2.5 mm, 14 faces (baked)
FEATURE [Part::Feature] Body002  label="Nozzle_0.4mm"
  Placement = pos=(0,-7,-15.5) rot=(0,0,1;0rad)
  shape: bbox 9.238 x 9.238 x 13 mm, 33 faces (baked)
FEATURE [Part::Feature] Body001082151  label="AluHeaterBlock"
  Placement = pos=(0,-7,-20) rot=(0,0,1;0rad)
  shape: bbox 19.8 x 20 x 10 mm, 37 faces (baked)
FEATURE [Part::Feature] Body008  label="M3x44-Screw_001"
  Placement = pos=(-10,-36.8,14.5) rot=(1,0,0;1.5708rad)
  shape: bbox 5.953 x 47 x 5.953 mm, 31 faces (baked)
FEATURE [Part::Feature] Fusion014  label="5015_CentrifugalFan"
  Placement = pos=(-22.5,3,8) rot=(0.57735,-0.57735,-0.57735;2.0944rad)
  shape: bbox 15 x 51.3 x 51.05 mm, 225 faces, 2 solids (baked)
FEATURE [Part::Feature] Body001082152  label="M3x44-Screw_002"
  Placement = pos=(22,-36.8,14.5) rot=(1,0,0;1.5708rad)
  shape: bbox 5.953 x 47 x 5.953 mm, 31 faces (baked)
FEATURE [Part::Feature] Compound007  label="4010_DC-Fan_001"
  Placement = pos=(6,-23.7,30.5) rot=(0,0,1;0rad)
  shape: bbox 40 x 18 x 40 mm, 120 faces, 2 solids (baked)
FEATURE [Part::Feature] Body001082153  label="HeatSink"
  Placement = pos=(6,-13,30) rot=(0,0,1;0rad)
  shape: bbox 40 x 10.7 x 40 mm, 117 faces (baked)
FEATURE [Part::Feature] Compound008  label="Nema17_38mm_001"
  Placement = pos=(6,3,30) rot=(0.57735,-0.57735,0.57735;2.0944rad)
  shape: bbox 42 x 61.2 x 54 mm, 83 faces, 8 solids (baked)
FEATURE [Part::Feature] Body001082154  label="FanDuct"
  Placement = pos=(-37.6,-7,-24.7) rot=(0,0,1;0rad)
  shape: bbox 22 x 16.8 x 39.7 mm, 26 faces (baked)
FEATURE [Part::Feature] Compound009  label="LM8LUU_004"
  Placement = pos=(0,40,0) rot=(0,1,0;1.5708rad)
  shape: bbox 45 x 15 x 15 mm, 36 faces, 2 solids (baked)
FEATURE [Part::Feature] Body001082155  label="5015_air-blower_holder"
  Placement = pos=(-22.5,-26.7,9.1) rot=(0,0,1;0rad)
  shape: bbox 4.5 x 58.6 x 59.7 mm, 16 faces (baked)
FEATURE [App::DocumentObjectGroup] Group025  label="part-cooling"
  Group = -> [Body001082155,Fusion014,Body001082154,Screw050,Screw051,Nut020,Nut021,Screw052,Screw046]
FEATURE [Part::Feature] Compound010  label="FanGrill"
  Placement = pos=(6,-35.5,30.5) rot=(0,0,1;3.14159rad)
  shape: bbox 40.12 x 4.644 x 40.12 mm, 34 faces, 4 solids (baked)
FEATURE [Part::Feature] Compound011  label="Extruder_MK8"
  Placement = pos=(6,3,30) rot=(0,0,1;0rad)
  shape: bbox 42.54 x 21.7 x 71.64 mm, 366 faces, 7 solids (baked)
FEATURE [App::DocumentObjectGroup] Group027  label="extruder"
  Group = -> [Compound008,Compound011]
FEATURE [Part::Feature] Compound006  label="TeflonThroatTube_40mm"
  Placement = pos=(0,-7,-15.5) rot=(0,0,1;0rad)
  shape: bbox 6 x 6 x 40 mm, 146 faces, 2 solids (baked)
FEATURE [App::DocumentObjectGroup] Group026  label="hotend"
  Group = -> [Compound006,Body002,Body001082151,Body001082153,Compound007,Compound010,Washer,Washer001,Body008,Body001082152]
FEATURE [Part::Feature] Compound012  label="micro switch 5A 125V 250V ~ 10T85u_001"
  Placement = pos=(-24.6,39.85,14.7) rot=(0,0,1;0rad)
  shape: bbox 24.69 x 20.93 x 6.4 mm, 78 faces, 4 solids (baked)
FEATURE [App::DocumentObjectGroup] Group024  label="carrier"
  Group = -> [Body001082149,Compound005,Compound009,Body001082150,Compound012,Screw053,Screw047,Screw049,Screw048]
FEATURE [App::Part] Part054  label="Printhead_assembly (Left/Right)"
  Group = -> [Body001082150,Compound009,Compound005,Body001082149,Compound012,Screw053,Screw049,Screw047,Screw048,Group024,Compound008,Compound011,Group027,Body008,Compound006,Body002,Body001082151,Body001082153,Compound007,Compound010,Body001082152,Washer001,Washer,Group026,Screw050,Screw052,Screw046,Nut020,Screw051,Nut021,Fusion014,Body001082155,Body001082154,Group025]
  Origin = -> Origin061
FEATURE [Part::Feature] Fusion001  label="StepperMotorNema17"
  Placement = pos=(-233.7,9,5.2e-14) rot=(0.57735,-0.57735,-0.57735;4.18879rad)
  shape: bbox 42 x 61.2 x 54 mm, 83 faces (baked)
FEATURE [App::Part] Part055  label="StepperMotorX"
  Group = -> [Fusion001]
  Origin = -> Origin062
FEATURE [Part::Feature] Fusion015  label="StepperMotorNema018"
  shape: bbox 54 x 42 x 61.2 mm, 83 faces (baked)
FEATURE [App::Part] Part056  label="StepperMotorL_Z"
  Group = -> [Fusion015]
  Origin = -> Origin063
  Placement = pos=(-180,-4e-16,35) rot=(0,0,1;1.5708rad)
FEATURE [Part::Feature] Compound013  label="Shaft_coupling_flex_D20L25_5/8_001"
  Placement = pos=(-180,0,50) rot=(0,0,1;0rad)
  shape: bbox 40.62 x 40.62 x 25 mm, 94 faces, 5 solids (baked)
FEATURE [Part::Feature] Compound014  label="Shaft_coupling_flex_D20L25_5/8_002"
  Placement = pos=(180,0,50) rot=(0,0,1;0rad)
  shape: bbox 40.62 x 40.62 x 25 mm, 94 faces, 5 solids (baked)
FEATURE [Part::Feature] Fusion016  label="StepperMotorNema019"
  shape: bbox 54 x 42 x 61.2 mm, 83 faces (baked)
FEATURE [App::Part] Part057  label="StepperMotorR_Z"
  Group = -> [Fusion016]
  Origin = -> Origin064
  Placement = pos=(180,-4e-16,35) rot=(0,0,1;1.5708rad)
FEATURE [Part::Feature] Body001082156  label="LeadScrew_TR8x8-L2_350_001"
  Placement = pos=(-180,0,64) rot=(0,0,1;0rad)
  shape: bbox 8 x 8 x 352 mm, 702 faces (baked)
FEATURE [Part::Feature] Body001082157  label="LeadScrew_TR8x8-L2_350_002"
  Placement = pos=(180,0,64) rot=(0,0,1;0rad)
  shape: bbox 8 x 8 x 352 mm, 702 faces (baked)
FEATURE [Part::Feature] Body001082158  label="D8x380_Rod003"
  Placement = pos=(-203,0,35) rot=(0,0,1;0rad)
  shape: bbox 8 x 8 x 380 mm, 5 faces (baked)
FEATURE [Part::Feature] Body001082159  label="D8x380_Rod004"
  Placement = pos=(203,0,35) rot=(0,0,1;0rad)
  shape: bbox 8 x 8 x 380 mm, 5 faces (baked)
FEATURE [Part::Feature] Body001  label="D8x445_Rod_001"
  Placement = pos=(226,40,0) rot=(0,-1,0;1.5708rad)
  shape: bbox 445 x 8 x 8 mm, 5 faces (baked)
FEATURE [Part::Feature] Body001082160  label="D8x445_Rod_002"
  Placement = pos=(226,-40,5e-14) rot=(0,-1,0;1.5708rad)
  shape: bbox 445 x 8 x 8 mm, 5 faces (baked)
FEATURE [App::DocumentObjectGroup] Group017  label="Guide&Drive-Unit_X"
  Group = -> [Part055,Body001,Body001082160]
FEATURE [App::Part] Part051  label="X-Axis"
  Group = -> [Group017,Part054,Part055,Body001,Body001082160]
  Origin = -> Origin057
FEATURE [App::Part] Part052  label="Z-axis cross beam_assembly  (up/down)"
  Group = -> [Part002,Part003,Part051]
  Origin = -> Origin059
  Placement = pos=(0,0,268.8) rot=(0,0,1;0rad)
FEATURE [Part::Feature] Compound015  label="nutblock_Item_springball_guide_slot5_M5_001"
  Placement = pos=(-186.5,61.8,22) rot=(1,0,0;3.14159rad)
  shape: bbox 7.7 x 5.15 x 12 mm, 24 faces, 2 solids (baked)
FEATURE [Part::Feature] Compound016  label="nutblock_Item_springball_guide_slot5_M5_002"
  Placement = pos=(-186.5,61.8,-7) rot=(0,0,1;3.14159rad)
  shape: bbox 7.7 x 5.15 x 12 mm, 24 faces, 2 solids (baked)
FEATURE [Part::Feature] Compound017  label="nutblock_Item_springball_guide_slot5_M5_003"
  Placement = pos=(-166.5,61.8,22) rot=(1,0,0;3.14159rad)
  shape: bbox 7.7 x 5.15 x 12 mm, 24 faces, 2 solids (baked)
FEATURE [Part::Feature] Compound018  label="nutblock_Item_springball_guide_slot5_M5_004"
  Placement = pos=(-166.5,61.8,-7) rot=(0,0,1;3.14159rad)
  shape: bbox 7.7 x 5.15 x 12 mm, 24 faces, 2 solids (baked)
FEATURE [Part::Feature] Body001082161  label="Z_Motor_Mount_L"
  Placement = pos=(-180,0,-20) rot=(0,0,1;0rad)
  shape: bbox 75 x 81.8 x 63 mm, 75 faces (baked)
FEATURE [Part::Feature] Body001082162  label="Z_Motor_Mount_R"
  Placement = pos=(180,0,-20) rot=(0,0,1;0rad)
  shape: bbox 75 x 81.8 x 63 mm, 75 faces (baked)
FEATURE [Part::Sphere] Sphere
  Angle1 = -90
  Angle2 = 90
  Angle3 = 360
  AttacherType = Attacher::AttachEngine3D
  Placement = pos=(-180,0,61.5) rot=(0,0,1;0rad)
  Radius = 2.5
FEATURE [Part::Sphere] Sphere001
  Angle1 = -90
  Angle2 = 90
  Angle3 = 360
  AttacherType = Attacher::AttachEngine3D
  Placement = pos=(180,0,61.5) rot=(0,0,1;0rad)
  Radius = 2.5
FEATURE [Part::Feature] Body001082163  label="Y_Rod_Holder_001"
  Placement = pos=(-85,-180,-4e-14) rot=(1,0,0;1.5708rad)
  shape: bbox 44 x 20 x 15 mm, 28 faces (baked)
FEATURE [Part::Feature] Body001082164  label="Y_Rod_Holder_002"
  Placement = pos=(85,-180,-4e-14) rot=(0,0.707107,0.707107;3.14159rad)
  shape: bbox 44 x 20 x 15 mm, 28 faces (baked)
FEATURE [Part::Feature] Body001082165  label="Y_Rod_Holder_003"
  Placement = pos=(-85,180,4e-14) rot=(1,0,0;1.5708rad)
  shape: bbox 44 x 20 x 15 mm, 28 faces (baked)
FEATURE [Part::Feature] Body001082166  label="Y_Rod_Holder_With_Endstop"
  Placement = pos=(85,180,1e-15) rot=(1,0,0;1.5708rad)
  shape: bbox 67 x 20 x 15 mm, 30 faces (baked)
FEATURE [Part::Feature] Compound019  label="Pulley_GT2-6mm-16T_bore_5_001"
  Placement = pos=(0,1.18e-14,18) rot=(0,0,1;0rad)
  shape: bbox 13 x 13 x 15 mm, 221 faces, 3 solids (baked)
FEATURE [App::Part] Part037  label="StepperMotorY"
  Group = -> [Fusion012,Compound019]
  Origin = -> Origin037
  Placement = pos=(-18,143.85,-6.4) rot=(0.57735,-0.57735,0.57735;4.18879rad)
FEATURE [Part::Feature] Compound020  label="idler-wheel_GT2-6mm-16T_bore_3_001"
  Placement = pos=(-1e-15,29.8,-5) rot=(0,-1,0;1.5708rad)
  shape: bbox 8.5 x 13 x 13 mm, 233 faces, 5 solids (baked)
FEATURE [Part::Feature] Body001082167  label="Y-Belt-Holder12mm001"
  Placement = pos=(0,0,8) rot=(0,0,1;0rad)
  shape: bbox 22 x 30 x 21 mm, 118 faces (baked)
FEATURE [App::DocumentObjectGroup] Group008  label="BeltClamp"
  Group = -> [Screw,Screw001,Screw002,Screw003,Body001082167]
FEATURE [App::DocumentObjectGroup] Group011  label="H-Holder001"
  Group = -> [Body001082125,Body001082127,Body001082126,Screw004,Screw005,Screw006,Screw007,Screw008,Screw009,Group008]
FEATURE [App::DocumentObjectGroup] Group010  label="carrying_frame"
  Group = -> [Group011,Group009]
FEATURE [App::Part] Part048  label="Y-Axis-Carrier_Assembly (front-back)"
  Group = -> [Group010,Body001082125,Body001082127,Body001082126,Group011,Group009,Part049,Part047,Part045,Part046,Group008,Screw,Screw001,Screw002,Screw003,Screw004,Screw005,Screw006,Screw007,Screw008,Screw009,Group012,Fusion013,Screw026,Screw027,Screw028,Screw029,Nut,Nut001,Nut002,Nut003,Body001082142,Body001082138,Body001082144,Body001082146,Body001082143,Body001082140,Body001082145,Body001082136,+1 more]
  Origin = -> Origin052
  Placement = pos=(0,0,7.9) rot=(0,0,1;0rad)
FEATURE [Part::Feature] Body001082170  label="Slider"
  Placement = pos=(0,12.3,-5) rot=(-1,0,0;1.5708rad)
  shape: bbox 32.31 x 25.61 x 32.85 mm, 39 faces (baked)
FEATURE [Part::Feature] Body001082171  label="KnurledWheel"
  Placement = pos=(0,2.1,-5) rot=(-1,0,0;1.5708rad)
  shape: bbox 40.19 x 20.41 x 40.19 mm, 226 faces (baked)
FEATURE [Part::FeaturePython] Nut022  label="M3-Nut076"  # Fasteners workbench fastener (typed FeaturePython)
  Placement = pos=(7.5,29.7651,-5.06051) rot=(0.694747,0.186157,0.694747;2.77349rad)
  diameter = 1
  invert = false
  matchOuter = false
  offset = 0
  thread = false
  type = 2
FEATURE [Part::FeaturePython] Screw054  label="M3x20-Screw"  # Fasteners workbench fastener (typed FeaturePython)
  Placement = pos=(-7.5,29.8,-5) rot=(0,-1,0;1.5708rad)
  diameter = 4
  invert = false
  length = 8
  matchOuter = false
  offset = 0
  thread = false
  type = 16
FEATURE [Part::Feature] Body001082169001  label="Frame001"
  Placement = pos=(0,0,0) rot=(0,0.707107,0.707107;3.14159rad)
  shape: bbox 64 x 40.8 x 55.8 mm, 59 faces (baked)
FEATURE [Part::Feature] Body001082169002  label="counterplate"
  Placement = pos=(3e-15,22.2,-5) rot=(0,0.707107,0.707107;3.14159rad)
  shape: bbox 55.38 x 3 x 49.38 mm, 21 faces (baked)
FEATURE [Part::Feature] Body001082169003  label="GT2-Belt_Y-Axis"
  Placement = pos=(0,0,-6.4) rot=(0,0,1;0rad)
  shape: bbox 6 x 295.1 x 11 mm, 10 faces (baked)
FEATURE [Part::Feature] Body001082169004  label="Z-Rod_Holder_R"
  Placement = pos=(203,0,420) rot=(0,0,1;0rad)
  shape: bbox 55 x 92.5 x 30 mm, 118 faces (baked)
FEATURE [Part::Feature] Body001082169005  label="Z-Rod_Holder_L"
  Placement = pos=(-203,0,420) rot=(0,0,1;0rad)
  shape: bbox 55 x 92.5 x 30 mm, 117 faces (baked)
FEATURE [App::DocumentObjectGroup] Group014  label="Guide&Drive-Unit_Z"
  Group = -> [Body001082158,Body001082159,Part056,Part057,Compound013,Compound014,Body001082156,Body001082157,Compound015,Compound016,Compound017,Compound018,Body001082161,Body001082162,Sphere,Sphere001,Body001082169004,Body001082169005]
FEATURE [App::Part] Part  label="ZX-Axis"
  Group = -> [Group014,Part052,Body001082158,Body001082159,Part056,Part057,Compound013,Compound014,Body001082156,Body001082157,Compound015,Compound016,Compound017,Compound018,Body001082161,Body001082162,Sphere,Sphere001,Body001082169004,Body001082169005]
  Origin = -> Origin
  Placement = pos=(0,3,0) rot=(0,0,1;0rad)
FEATURE [Part::Feature] Body001082001  label="Y_MotorMount"
  Placement = pos=(-18,170,-40) rot=(0,0,1;0rad)
  shape: bbox 74 x 47.3 x 54.75 mm, 52 faces (baked)
FEATURE [Part::Feature] Body001082169006  label="Y-Tensioner_Frame"
  Placement = pos=(0,0,-5) rot=(0,0,1;3.14159rad)
  shape: bbox 68 x 22.2 x 51.35 mm, 43 faces (baked)
FEATURE [App::Part] Part058  label="Y-Axis-Tensioner"
  Group = -> [Body001082171,Body001082170,Compound020,Nut022,Screw054,Body001082169001,Body001082169002,Body001082169006]
  Origin = -> Origin065
  Placement = pos=(0,-170,-1.4) rot=(0,0,1;0rad)
FEATURE [App::DocumentObjectGroup] Group023  label="Guide&Drive-Unit_Y"
  Group = -> [Body001053,Body001054,Part037,Fusion011,Body001082002,Body001082163,Body001082164,Body001082165,Body001082166,Part058,Body001082169003,Body001082001]
FEATURE [App::Part] Part053  label="Y-Axis"
  Group = -> [Body001082002,Body001053,Body001054,Fusion011,Part037,Group023,Part048,Body001082163,Body001082164,Body001082165,Body001082166,Part058,Body001082169003,Body001082001]
  Origin = -> Origin060
  Placement = pos=(0,0,20) rot=(0,0,1;0rad)
FEATURE [Part::Feature] Compound021  label="PowerSupply_S-240-12"
  Placement = pos=(168,145.35,151) rot=(0,1,0;1.5708rad)
  shape: bbox 77.73 x 187.7 x 221.8 mm, 2572 faces, 37 solids (baked)
FEATURE [Part::Feature] Compound022  label="Power inlet IEC 320 C14"
  Placement = pos=(187,203,14.5) rot=(-0.57735,-0.57735,-0.57735;2.0944rad)
  shape: bbox 49.5 x 34.17 x 59 mm, 542 faces, 17 solids (baked)
FEATURE [Part::Feature] Body001001  label="PSU_Cover"
  shape: bbox 58.4 x 120 x 98 mm, 71 faces (baked)
FEATURE [Part::Feature] Body001082169007  label="PSU-Mount"
  shape: bbox 23 x 129.7 x 140 mm, 70 faces (baked)
FEATURE [App::DocumentObjectGroup] Group022  label="Electronic"
  Group = -> [Body001001,Body001082169007,Compound022,Compound021]
